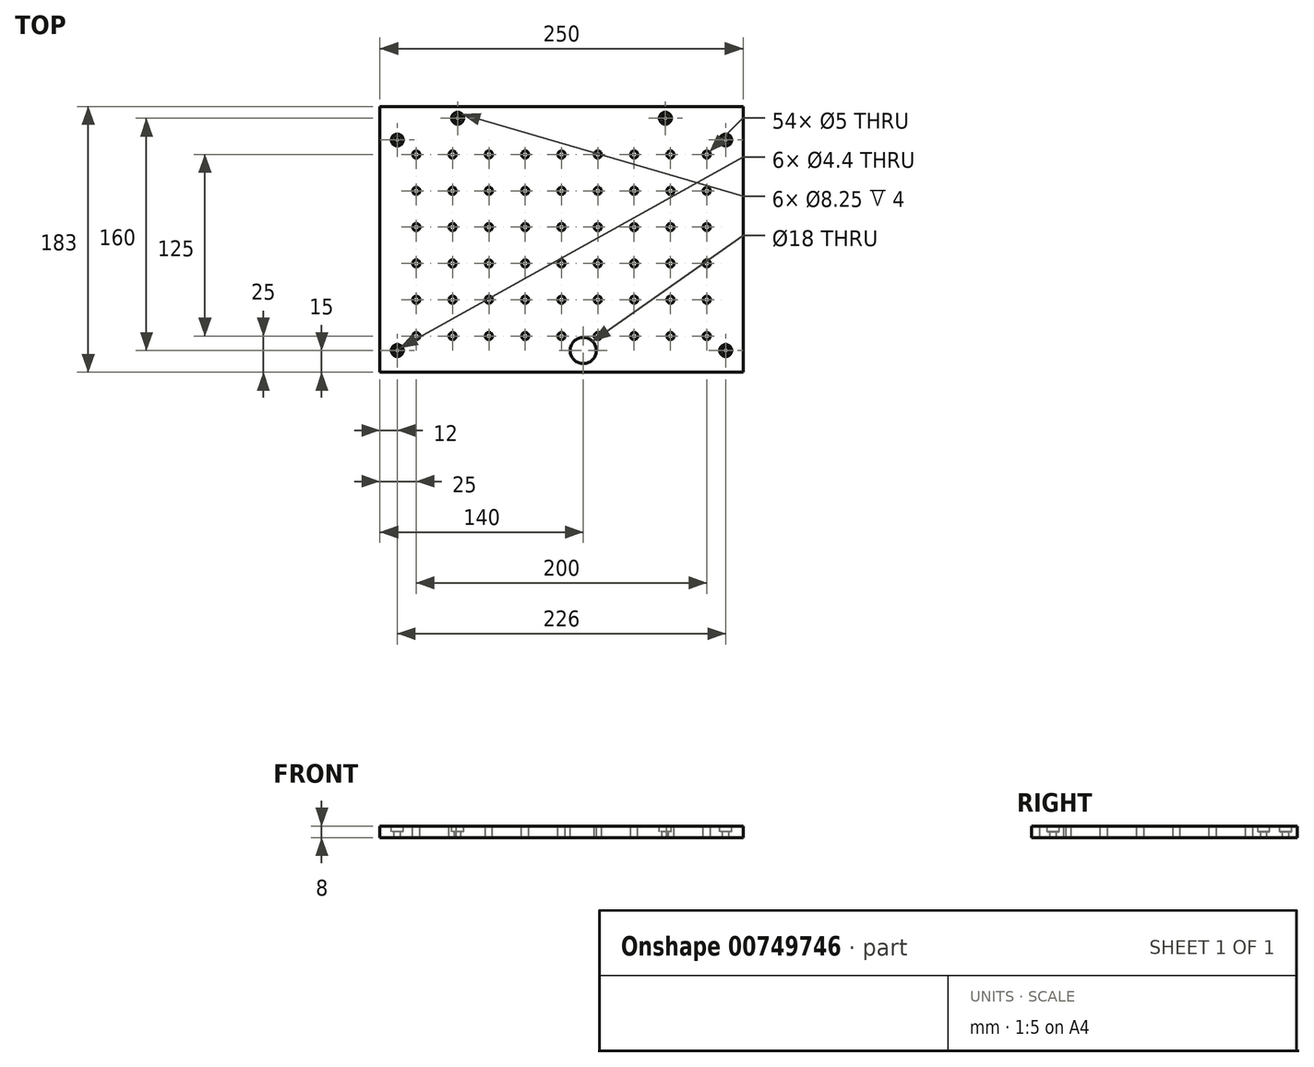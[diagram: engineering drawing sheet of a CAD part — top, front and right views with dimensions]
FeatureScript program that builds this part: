
annotation { "Feature Type Name" : "Feature", "Feature Type Description" : "" }
export const myFeature = defineFeature(function(context is Context, id is Id, definition is map)
    precondition{}
    {
        {
            var Q0;
            Q0=qCreatedBy(makeId("Top.planeOp"),FACE);
            var sketch = newSketch(context, id + "F0", { "sketchPlane" : qUnion([Q0])});
            skLineSegment(sketch, "E0.bottom", {"start": v(125, -91.5) * mm, "end": v(-125, -91.5) * mm});
            skLineSegment(sketch, "E0.top", {"start": v(125, 91.5) * mm, "end": v(-125, 91.5) * mm});
            skLineSegment(sketch, "E0.left", {"start": v(125, -91.5) * mm, "end": v(125, 91.5) * mm});
            skLineSegment(sketch, "E0.right", {"start": v(-125, -91.5) * mm, "end": v(-125, 91.5) * mm});
            skPoint(sketch, "E0.middle", {"position": v(0, 0) * mm});
            skSolve(sketch);
        }
        {
            var Q0;
            Q0 = qSketchRegion(id + "F0", true);
            extrude(context, id + "F1", {"entities" : qUnion([Q0]), "depth" : 8 * mm, "offsetDistance" : 25 * mm});
        }
        {
            var Q0;
            Q0=makeQuery(id+"F1.opExtrude","CAP_FACE",FACE,{"disambiguationData":[OSD([sQuery(id+"F0.wireOp",EDGE,"E0.bottom"),sQuery(id+"F0.wireOp",EDGE,"E0.top"),sQuery(id+"F0.wireOp",EDGE,"E0.left"),sQuery(id+"F0.wireOp",EDGE,"E0.right")])],"isStart":false});
            var sketch = newSketch(context, id + "F2", { "sketchPlane" : qUnion([Q0])});
            skLineSegment(sketch, "E1.bottom", {"start": v(-113, 68.5) * mm, "end": v(113, 68.5) * mm, "construction": true});
            skLineSegment(sketch, "E1.top", {"start": v(-113, -76.5) * mm, "end": v(113, -76.5) * mm, "construction": true});
            skLineSegment(sketch, "E1.left", {"start": v(-113, 68.5) * mm, "end": v(-113, -76.5) * mm, "construction": true});
            skLineSegment(sketch, "E1.right", {"start": v(113, 68.5) * mm, "end": v(113, -76.5) * mm, "construction": true});
            skLineSegment(sketch, "E2", {"start": v(-71.5, 83.5) * mm, "end": v(71.5, 83.5) * mm, "construction": true});
            skPoint(sketch, "E3", {"position": v(15, -76.5) * mm});
            skPoint(sketch, "E4", {"position": v(-100, -66.5) * mm});
            skPoint(sketch, "E5.0.1.0", {"position": v(-100, -41.5) * mm});
            skPoint(sketch, "E5.0.2.0", {"position": v(-100, -16.5) * mm});
            skPoint(sketch, "E5.0.3.0", {"position": v(-100, 8.5) * mm});
            skPoint(sketch, "E5.0.4.0", {"position": v(-100, 33.5) * mm});
            skPoint(sketch, "E5.0.5.0", {"position": v(-100, 58.5) * mm});
            skPoint(sketch, "E5.1.0.0", {"position": v(-75, -66.5) * mm});
            skPoint(sketch, "E5.1.1.0", {"position": v(-75, -41.5) * mm});
            skPoint(sketch, "E5.1.2.0", {"position": v(-75, -16.5) * mm});
            skPoint(sketch, "E5.1.3.0", {"position": v(-75, 8.5) * mm});
            skPoint(sketch, "E5.1.4.0", {"position": v(-75, 33.5) * mm});
            skPoint(sketch, "E5.1.5.0", {"position": v(-75, 58.5) * mm});
            skPoint(sketch, "E5.2.0.0", {"position": v(-50, -66.5) * mm});
            skPoint(sketch, "E5.2.1.0", {"position": v(-50, -41.5) * mm});
            skPoint(sketch, "E5.2.2.0", {"position": v(-50, -16.5) * mm});
            skPoint(sketch, "E5.2.3.0", {"position": v(-50, 8.5) * mm});
            skPoint(sketch, "E5.2.4.0", {"position": v(-50, 33.5) * mm});
            skPoint(sketch, "E5.2.5.0", {"position": v(-50, 58.5) * mm});
            skPoint(sketch, "E5.3.0.0", {"position": v(-25, -66.5) * mm});
            skPoint(sketch, "E5.3.1.0", {"position": v(-25, -41.5) * mm});
            skPoint(sketch, "E5.3.2.0", {"position": v(-25, -16.5) * mm});
            skPoint(sketch, "E5.3.3.0", {"position": v(-25, 8.5) * mm});
            skPoint(sketch, "E5.3.4.0", {"position": v(-25, 33.5) * mm});
            skPoint(sketch, "E5.3.5.0", {"position": v(-25, 58.5) * mm});
            skPoint(sketch, "E5.4.0.0", {"position": v(0, -66.5) * mm});
            skPoint(sketch, "E5.4.1.0", {"position": v(0, -41.5) * mm});
            skPoint(sketch, "E5.4.2.0", {"position": v(0, -16.5) * mm});
            skPoint(sketch, "E5.4.3.0", {"position": v(0, 8.5) * mm});
            skPoint(sketch, "E5.4.4.0", {"position": v(0, 33.5) * mm});
            skPoint(sketch, "E5.4.5.0", {"position": v(0, 58.5) * mm});
            skPoint(sketch, "E5.5.0.0", {"position": v(25, -66.5) * mm});
            skPoint(sketch, "E5.5.1.0", {"position": v(25, -41.5) * mm});
            skPoint(sketch, "E5.5.2.0", {"position": v(25, -16.5) * mm});
            skPoint(sketch, "E5.5.3.0", {"position": v(25, 8.5) * mm});
            skPoint(sketch, "E5.5.4.0", {"position": v(25, 33.5) * mm});
            skPoint(sketch, "E5.5.5.0", {"position": v(25, 58.5) * mm});
            skPoint(sketch, "E5.6.0.0", {"position": v(50, -66.5) * mm});
            skPoint(sketch, "E5.6.1.0", {"position": v(50, -41.5) * mm});
            skPoint(sketch, "E5.6.2.0", {"position": v(50, -16.5) * mm});
            skPoint(sketch, "E5.6.3.0", {"position": v(50, 8.5) * mm});
            skPoint(sketch, "E5.6.4.0", {"position": v(50, 33.5) * mm});
            skPoint(sketch, "E5.6.5.0", {"position": v(50, 58.5) * mm});
            skPoint(sketch, "E5.7.0.0", {"position": v(75, -66.5) * mm});
            skPoint(sketch, "E5.7.1.0", {"position": v(75, -41.5) * mm});
            skPoint(sketch, "E5.7.2.0", {"position": v(75, -16.5) * mm});
            skPoint(sketch, "E5.7.3.0", {"position": v(75, 8.5) * mm});
            skPoint(sketch, "E5.7.4.0", {"position": v(75, 33.5) * mm});
            skPoint(sketch, "E5.7.5.0", {"position": v(75, 58.5) * mm});
            skPoint(sketch, "E5.8.0.0", {"position": v(100, -66.5) * mm});
            skPoint(sketch, "E5.8.1.0", {"position": v(100, -41.5) * mm});
            skPoint(sketch, "E5.8.2.0", {"position": v(100, -16.5) * mm});
            skPoint(sketch, "E5.8.3.0", {"position": v(100, 8.5) * mm});
            skPoint(sketch, "E5.8.4.0", {"position": v(100, 33.5) * mm});
            skPoint(sketch, "E5.8.5.0", {"position": v(100, 58.5) * mm});
            skLineSegment(sketch, "E5.direction1", {"start": v(-100, -66.5) * mm, "end": v(-75, -66.5) * mm, "construction": true});
            skLineSegment(sketch, "E5.direction2", {"start": v(-100, -66.5) * mm, "end": v(-100, -41.5) * mm, "construction": true});
            skLineSegment(sketch, "E6.direction1", {"start": v(-52.8, 83.5) * mm, "end": v(-25, 83.5) * mm, "construction": true});
            skSolve(sketch);
        }
        {
            var Q0;
            Q0=sQuery(id+"F2.wireOp",VERTEX,"E1.left.start");
            var Q1;
            Q1=sQuery(id+"F2.wireOp",VERTEX,"E1.left.end");
            var Q2;
            Q2=sQuery(id+"F2.wireOp",VERTEX,"E1.top.end");
            var Q3;
            Q3=sQuery(id+"F2.wireOp",VERTEX,"E1.right.start");
            var Q4;
            Q4=sQuery(id+"F2.wireOp",VERTEX,"E2.end");
            var Q5;
            Q5=sQuery(id+"F2.wireOp",VERTEX,"E2.start");
            var Q6;
            Q6=makeQuery(id+"F1.opExtrude","SWEPT_BODY",BODY,{"disambiguationData":[OSD([sQuery(id+"F0.wireOp",EDGE,"E0.bottom"),sQuery(id+"F0.wireOp",EDGE,"E0.top"),sQuery(id+"F0.wireOp",EDGE,"E0.left"),sQuery(id+"F0.wireOp",EDGE,"E0.right")])]});
            hole(context, id + "F3", {"style" : HoleStyle.C_BORE, "endStyle" : HoleEndStyle.THROUGH, "standardTappedOrClearance" : lookupTablePath({ "standard" : "ISO", "fit" : "Normal", "size" : "M4", "type" : "Clearance" }), "standardBlindInLast" : lookupTablePath({ "fit" : "Standard", "standard" : "ISO", "size" : "M4", "type" : "Clearance" }), "holeDiameter" : 4.4 * mm, "cBoreDiameter" : 8.25 * mm, "cBoreDepth" : 4 * mm, "majorDiameter" : 5 * mm, "isTappedThrough" : true, "tappedDepth" : 12 * mm, "tapClearance" : 3, "locations" : qUnion([Q0, Q1, Q2, Q3, Q4, Q5]), "scope" : qUnion([Q6])});
        }
        {
            var Q0;
            Q0=sQuery(id+"F2.wireOp",VERTEX,"E3");
            var Q1;
            Q1=makeQuery(id+"F1.opExtrude","SWEPT_BODY",BODY,{"disambiguationData":[OSD([sQuery(id+"F0.wireOp",EDGE,"E0.bottom"),sQuery(id+"F0.wireOp",EDGE,"E0.top"),sQuery(id+"F0.wireOp",EDGE,"E0.left"),sQuery(id+"F0.wireOp",EDGE,"E0.right")])]});
            hole(context, id + "F4", {"style" : HoleStyle.SIMPLE, "endStyle" : HoleEndStyle.THROUGH, "holeDiameter" : 18 * mm, "majorDiameter" : 5 * mm, "isTappedThrough" : true, "tappedDepth" : 12 * mm, "tapClearance" : 3, "locations" : qUnion([Q0]), "scope" : qUnion([Q1])});
        }
        {
            var Q0;
            Q0=sQuery(id+"F2.wireOp",VERTEX,"3700d446-4044-4a76-a638-d8f890425de1");
            var Q1;
            Q1=sQuery(id+"F2.wireOp",VERTEX,"E5.8.5.0");
            var Q2;
            Q2=sQuery(id+"F2.wireOp",VERTEX,"E5.8.4.0");
            var Q3;
            Q3=sQuery(id+"F2.wireOp",VERTEX,"E5.8.3.0");
            var Q4;
            Q4=sQuery(id+"F2.wireOp",VERTEX,"E5.8.2.0");
            var Q5;
            Q5=sQuery(id+"F2.wireOp",VERTEX,"E5.8.1.0");
            var Q6;
            Q6=sQuery(id+"F2.wireOp",VERTEX,"E5.8.0.0");
            var Q7;
            Q7=sQuery(id+"F2.wireOp",VERTEX,"E5.7.0.0");
            var Q8;
            Q8=sQuery(id+"F2.wireOp",VERTEX,"E5.7.1.0");
            var Q9;
            Q9=sQuery(id+"F2.wireOp",VERTEX,"E5.7.2.0");
            var Q10;
            Q10=sQuery(id+"F2.wireOp",VERTEX,"E5.7.3.0");
            var Q11;
            Q11=sQuery(id+"F2.wireOp",VERTEX,"E5.7.4.0");
            var Q12;
            Q12=sQuery(id+"F2.wireOp",VERTEX,"E5.7.5.0");
            var Q13;
            Q13=sQuery(id+"F2.wireOp",VERTEX,"E6.4.0.0");
            var Q14;
            Q14=sQuery(id+"F2.wireOp",VERTEX,"E5.6.5.0");
            var Q15;
            Q15=sQuery(id+"F2.wireOp",VERTEX,"E5.6.4.0");
            var Q16;
            Q16=sQuery(id+"F2.wireOp",VERTEX,"E5.6.3.0");
            var Q17;
            Q17=sQuery(id+"F2.wireOp",VERTEX,"E5.6.2.0");
            var Q18;
            Q18=sQuery(id+"F2.wireOp",VERTEX,"E5.6.1.0");
            var Q19;
            Q19=sQuery(id+"F2.wireOp",VERTEX,"E5.6.0.0");
            var Q20;
            Q20=sQuery(id+"F2.wireOp",VERTEX,"E5.5.0.0");
            var Q21;
            Q21=sQuery(id+"F2.wireOp",VERTEX,"E5.4.0.0");
            var Q22;
            Q22=sQuery(id+"F2.wireOp",VERTEX,"E5.3.0.0");
            var Q23;
            Q23=sQuery(id+"F2.wireOp",VERTEX,"E5.2.0.0");
            var Q24;
            Q24=sQuery(id+"F2.wireOp",VERTEX,"E5.1.0.0");
            var Q25;
            Q25=sQuery(id+"F2.wireOp",VERTEX,"E4");
            var Q26;
            Q26=sQuery(id+"F2.wireOp",VERTEX,"E5.0.1.0");
            var Q27;
            Q27=sQuery(id+"F2.wireOp",VERTEX,"E5.1.1.0");
            var Q28;
            Q28=sQuery(id+"F2.wireOp",VERTEX,"E5.2.1.0");
            var Q29;
            Q29=sQuery(id+"F2.wireOp",VERTEX,"E5.3.1.0");
            var Q30;
            Q30=sQuery(id+"F2.wireOp",VERTEX,"E5.4.1.0");
            var Q31;
            Q31=sQuery(id+"F2.wireOp",VERTEX,"E5.5.1.0");
            var Q32;
            Q32=sQuery(id+"F2.wireOp",VERTEX,"E5.5.2.0");
            var Q33;
            Q33=sQuery(id+"F2.wireOp",VERTEX,"E5.4.2.0");
            var Q34;
            Q34=sQuery(id+"F2.wireOp",VERTEX,"E5.3.2.0");
            var Q35;
            Q35=sQuery(id+"F2.wireOp",VERTEX,"E5.2.2.0");
            var Q36;
            Q36=sQuery(id+"F2.wireOp",VERTEX,"E5.1.2.0");
            var Q37;
            Q37=sQuery(id+"F2.wireOp",VERTEX,"E5.0.2.0");
            var Q38;
            Q38=sQuery(id+"F2.wireOp",VERTEX,"E5.0.3.0");
            var Q39;
            Q39=sQuery(id+"F2.wireOp",VERTEX,"E5.1.3.0");
            var Q40;
            Q40=sQuery(id+"F2.wireOp",VERTEX,"E5.2.3.0");
            var Q41;
            Q41=sQuery(id+"F2.wireOp",VERTEX,"E5.3.3.0");
            var Q42;
            Q42=sQuery(id+"F2.wireOp",VERTEX,"E5.4.3.0");
            var Q43;
            Q43=sQuery(id+"F2.wireOp",VERTEX,"E5.5.3.0");
            var Q44;
            Q44=sQuery(id+"F2.wireOp",VERTEX,"E5.5.4.0");
            var Q45;
            Q45=sQuery(id+"F2.wireOp",VERTEX,"E5.4.4.0");
            var Q46;
            Q46=sQuery(id+"F2.wireOp",VERTEX,"E5.3.4.0");
            var Q47;
            Q47=sQuery(id+"F2.wireOp",VERTEX,"E5.2.4.0");
            var Q48;
            Q48=sQuery(id+"F2.wireOp",VERTEX,"E5.1.4.0");
            var Q49;
            Q49=sQuery(id+"F2.wireOp",VERTEX,"E5.0.4.0");
            var Q50;
            Q50=sQuery(id+"F2.wireOp",VERTEX,"E5.0.5.0");
            var Q51;
            Q51=sQuery(id+"F2.wireOp",VERTEX,"38ebba2f-137a-4872-a635-52bcc81825fb");
            var Q52;
            Q52=sQuery(id+"F2.wireOp",VERTEX,"E5.1.5.0");
            var Q53;
            Q53=sQuery(id+"F2.wireOp",VERTEX,"E5.2.5.0");
            var Q54;
            Q54=sQuery(id+"F2.wireOp",VERTEX,"732aa9ee-ac56-46f8-a658-cc575965ac6a");
            var Q55;
            Q55=sQuery(id+"F2.wireOp",VERTEX,"E6.1.0.0");
            var Q56;
            Q56=sQuery(id+"F2.wireOp",VERTEX,"E6.3.0.0");
            var Q57;
            Q57=sQuery(id+"F2.wireOp",VERTEX,"E5.5.5.0");
            var Q58;
            Q58=sQuery(id+"F2.wireOp",VERTEX,"E5.3.5.0");
            var Q59;
            Q59=sQuery(id+"F2.wireOp",VERTEX,"E5.4.5.0");
            var Q60;
            Q60=sQuery(id+"F2.wireOp",VERTEX,"E6.2.0.0");
            var Q61;
            Q61=makeQuery(id+"F1.opExtrude","SWEPT_BODY",BODY,{"disambiguationData":[OSD([sQuery(id+"F0.wireOp",EDGE,"E0.bottom"),sQuery(id+"F0.wireOp",EDGE,"E0.top"),sQuery(id+"F0.wireOp",EDGE,"E0.left"),sQuery(id+"F0.wireOp",EDGE,"E0.right")])]});
            hole(context, id + "F5", {"style" : HoleStyle.SIMPLE, "endStyle" : HoleEndStyle.THROUGH, "standardTappedOrClearance" : lookupTablePath({ "standard" : "ISO", "engagement" : "75%", "pitch" : "1 mm", "size" : "M6", "type" : "Tapped" }), "standardBlindInLast" : lookupTablePath({ "standard" : "ISO", "engagement" : "75%", "pitch" : "1 mm", "size" : "M6", "type" : "Tapped" }), "holeDiameter" : 5 * mm, "majorDiameter" : 6 * mm, "showTappedDepth" : true, "isTappedThrough" : true, "tappedDepth" : 12 * mm, "tapClearance" : 3, "locations" : qUnion([Q0, Q1, Q2, Q3, Q4, Q5, Q6, Q7, Q8, Q9, Q10, Q11, Q12, Q13, Q14, Q15, Q16, Q17, Q18, Q19, Q20, Q21, Q22, Q23, Q24, Q25, Q26, Q27, Q28, Q29, Q30, Q31, Q32, Q33, Q34, Q35, Q36, Q37, Q38, Q39, Q40, Q41, Q42, Q43, Q44, Q45, Q46, Q47, Q48, Q49, Q50, Q51, Q52, Q53, Q54, Q55, Q56, Q57, Q58, Q59, Q60]), "scope" : qUnion([Q61])});
        }
    });
